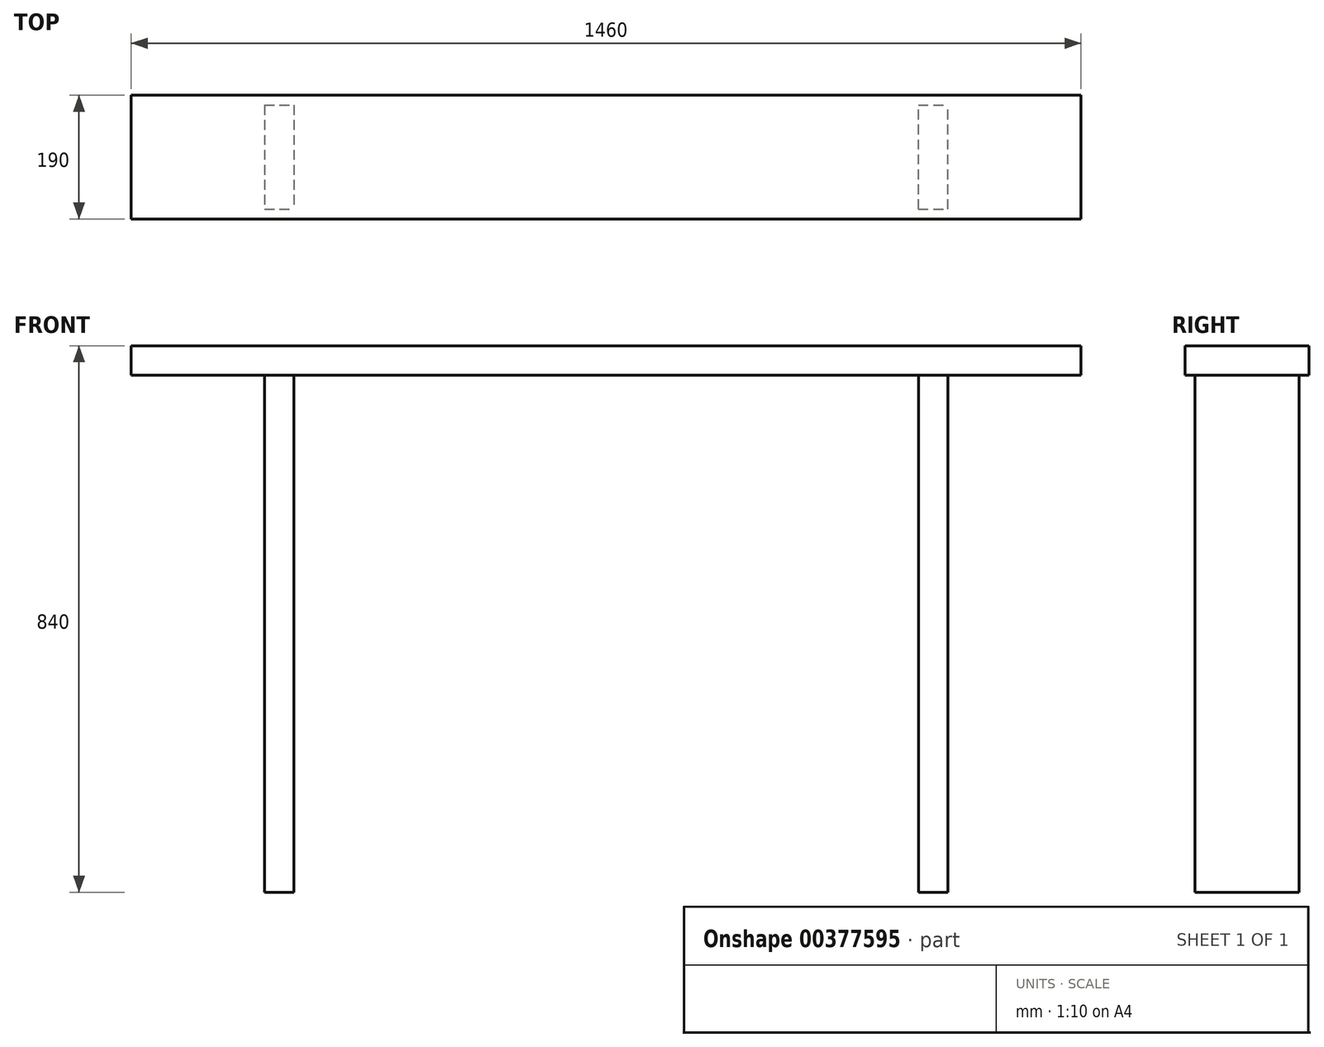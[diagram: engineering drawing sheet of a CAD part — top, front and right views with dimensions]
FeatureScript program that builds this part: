
annotation { "Feature Type Name" : "Feature", "Feature Type Description" : "" }
export const myFeature = defineFeature(function(context is Context, id is Id, definition is map)
    precondition{}
    {
        {
            var Q0;
            Q0=qCreatedBy(makeId("Top.planeOp"),FACE);
            var sketch = newSketch(context, id + "F0", { "sketchPlane" : qUnion([Q0])});
            skLineSegment(sketch, "E0.bottom", {"start": v(-730, 95) * mm, "end": v(730, 95) * mm});
            skLineSegment(sketch, "E0.top", {"start": v(-730, -95) * mm, "end": v(730, -95) * mm});
            skLineSegment(sketch, "E0.left", {"start": v(-730, 95) * mm, "end": v(-730, -95) * mm});
            skLineSegment(sketch, "E0.right", {"start": v(730, 95) * mm, "end": v(730, -95) * mm});
            skPoint(sketch, "E0.middle", {"position": v(0, 0) * mm});
            skSolve(sketch);
        }
        {
            var Q0;
            Q0 = qSketchRegion(id + "F0", true);
            extrude(context, id + "F1", {"entities" : qUnion([Q0]), "depth" : 45 * mm});
        }
        {
            var Q0;
            Q0=makeQuery(id+"F1.opExtrude","CAP_FACE",FACE,{"disambiguationData":[OSD([sQuery(id+"F0.wireOp",EDGE,"E0.bottom"),sQuery(id+"F0.wireOp",EDGE,"E0.top"),sQuery(id+"F0.wireOp",EDGE,"E0.left"),sQuery(id+"F0.wireOp",EDGE,"E0.right")])],"isStart":true});
            var sketch = newSketch(context, id + "F2", { "sketchPlane" : qUnion([Q0])});
            skLineSegment(sketch, "E1", {"start": v(-502.5, 0) * mm, "end": v(502.5, 0) * mm, "construction": true});
            skLineSegment(sketch, "E2.bottom", {"start": v(-525, -80) * mm, "end": v(-480, -80) * mm});
            skLineSegment(sketch, "E2.top", {"start": v(-525, 80) * mm, "end": v(-480, 80) * mm});
            skLineSegment(sketch, "E2.left", {"start": v(-525, -80) * mm, "end": v(-525, 80) * mm});
            skLineSegment(sketch, "E2.right", {"start": v(-480, -80) * mm, "end": v(-480, 80) * mm});
            skPoint(sketch, "E2.middle", {"position": v(-502.5, 0) * mm});
            skLineSegment(sketch, "E3.bottom", {"start": v(480, 80) * mm, "end": v(525, 80) * mm});
            skLineSegment(sketch, "E3.top", {"start": v(480, -80) * mm, "end": v(525, -80) * mm});
            skLineSegment(sketch, "E3.left", {"start": v(480, 80) * mm, "end": v(480, -80) * mm});
            skLineSegment(sketch, "E3.right", {"start": v(525, 80) * mm, "end": v(525, -80) * mm});
            skPoint(sketch, "E3.middle", {"position": v(502.5, 0) * mm});
            skSolve(sketch);
        }
        {
            var Q0;
            Q0 = qSketchRegion(id + "F2", true);
            extrude(context, id + "F3", {"entities" : qUnion([Q0]), "operationType" : NewBodyOperationType.ADD, "depth" : 795 * mm});
        }
    });
